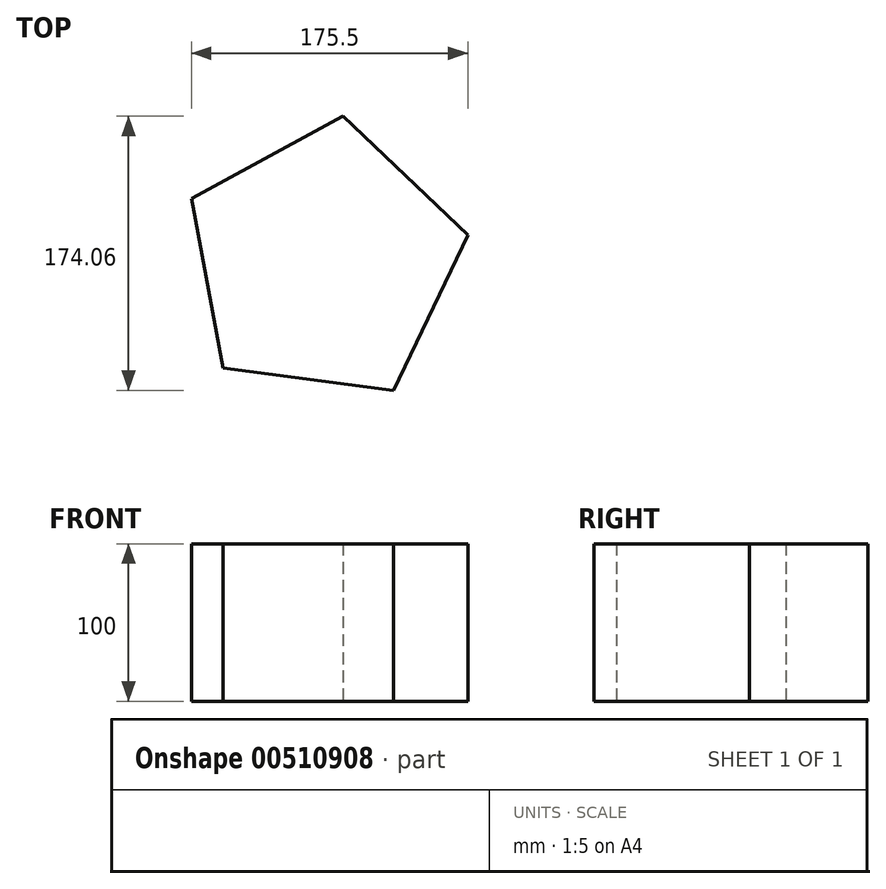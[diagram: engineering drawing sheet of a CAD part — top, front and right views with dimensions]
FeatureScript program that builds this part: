
annotation { "Feature Type Name" : "Feature", "Feature Type Description" : "" }
export const myFeature = defineFeature(function(context is Context, id is Id, definition is map)
    precondition{}
    {
        {
            var Q0;
            Q0=qCreatedBy(makeId("Top.planeOp"),FACE);
            var sketch = newSketch(context, id + "F0", { "sketchPlane" : qUnion([Q0])});
            skCircle(sketch, "E0.cCircle", {"center": v(0, 0) * mm, "radius": 93.06 * mm, "construction": true});
            skLineSegment(sketch, "E0.0", {"start": v(44.39, -81.8) * mm, "end": v(-64.07, -67.5) * mm});
            skLineSegment(sketch, "E0.1", {"start": v(-64.07, -67.5) * mm, "end": v(-83.99, 40.08) * mm});
            skLineSegment(sketch, "E0.2", {"start": v(-83.99, 40.08) * mm, "end": v(12.17, 92.26) * mm});
            skLineSegment(sketch, "E0.3", {"start": v(12.17, 92.26) * mm, "end": v(91.5, 16.94) * mm});
            skLineSegment(sketch, "E0.4", {"start": v(91.5, 16.94) * mm, "end": v(44.39, -81.8) * mm});
            skSolve(sketch);
        }
        {
            var Q0;
            Q0 = qSketchRegion(id + "F0", true);
            extrude(context, id + "F1", {"entities" : qUnion([Q0]), "depth" : 100 * mm});
        }
    });
